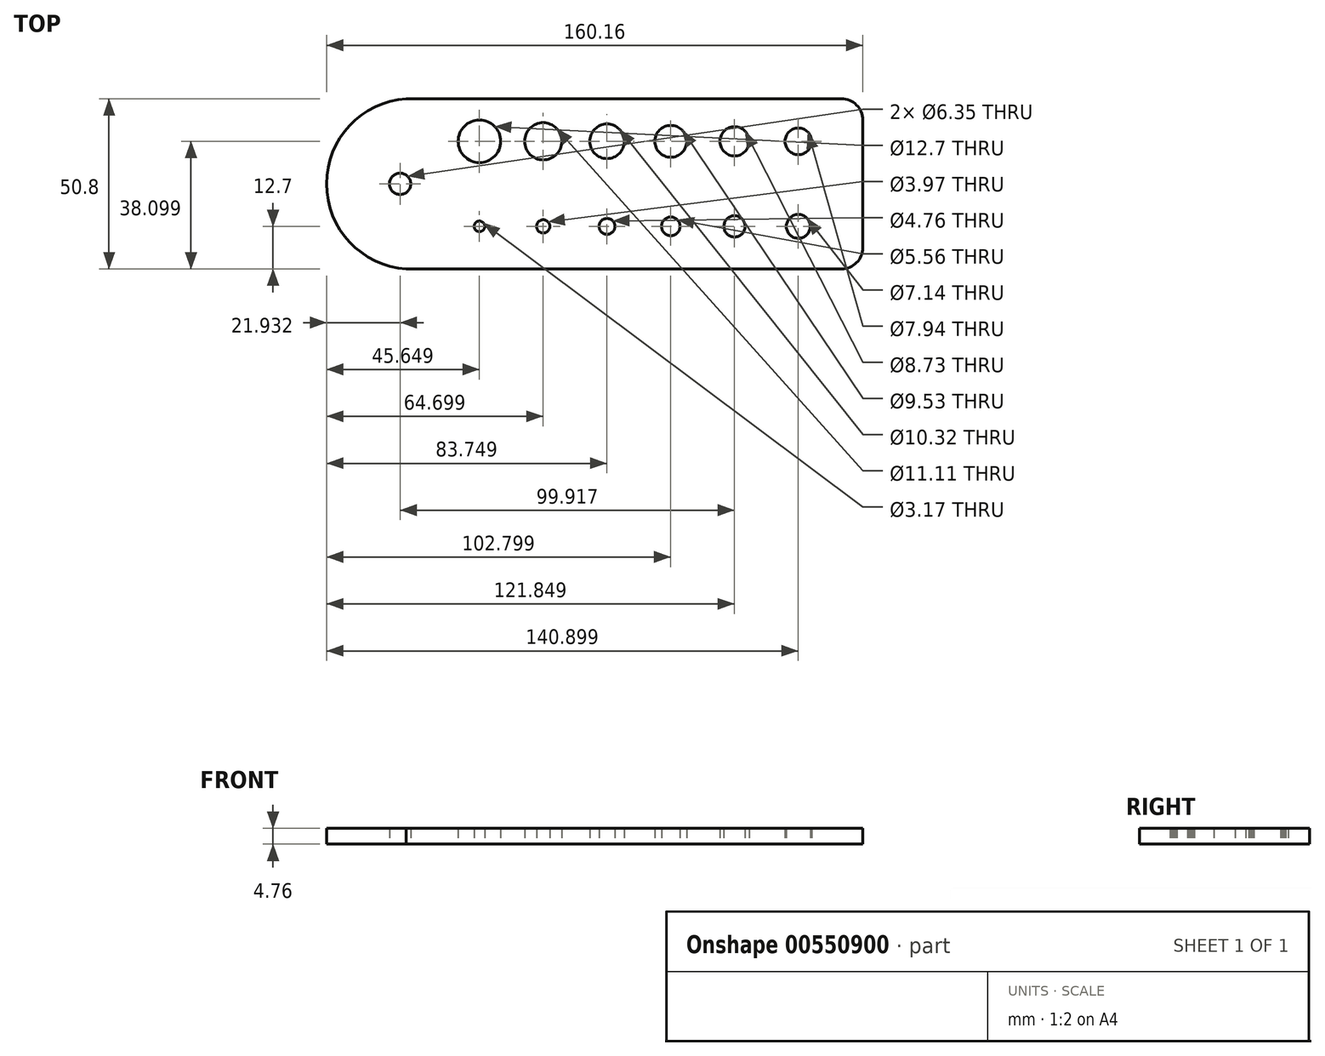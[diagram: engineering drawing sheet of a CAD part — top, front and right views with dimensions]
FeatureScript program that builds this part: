
annotation { "Feature Type Name" : "Feature", "Feature Type Description" : "" }
export const myFeature = defineFeature(function(context is Context, id is Id, definition is map)
    precondition{}
    {
        {
            var Q0;
            Q0=qCreatedBy(makeId("Top.planeOp"),FACE);
            var sketch = newSketch(context, id + "F0", { "sketchPlane" : qUnion([Q0])});
            skLineSegment(sketch, "E0.bottom", {"start": v(-46.8, 40.45) * mm, "end": v(83.22, 40.45) * mm});
            skLineSegment(sketch, "E0.top", {"start": v(-46.8, -10.35) * mm, "end": v(83.22, -10.35) * mm});
            skLineSegment(sketch, "E0.left", {"start": v(-62.83, 33.35) * mm, "end": v(-62.83, 33.35) * mm});
            skLineSegment(sketch, "E0.right", {"start": v(89.57, 34.1) * mm, "end": v(89.57, -4) * mm});
            skArc(sketch, "E1", {"start": v(-46.8, 40.45) * mm, "mid": v(-70.59, 15.05) * mm, "end": v(-46.8, -10.35) * mm});
            skPoint(sketch, "E2.visualSharp", {"position": v(89.57, -10.35) * mm});
            skArc(sketch, "E2.filletArc", {"start": v(83.22, -10.35) * mm, "mid": v(87.71, -8.5) * mm, "end": v(89.57, -4) * mm});
            skPoint(sketch, "E3.visualSharp", {"position": v(89.57, 40.45) * mm});
            skArc(sketch, "E3.filletArc", {"start": v(89.57, 34.1) * mm, "mid": v(87.71, 38.59) * mm, "end": v(83.22, 40.45) * mm});
            skSolve(sketch);
        }
        {
            var Q0;
            {var subQ5=sQuery(id+"F0.wireOp",EDGE,"E0.bottom");Q0=makeQuery(id+"F0.imprint","IMPRINT",FACE,{"disambiguationData":[TD([[makeQuery(id+"F0.imprint","IMPRINT",EDGE,{"derivedFrom":subQ5}),-1.0]])]});}
            var sketch = newSketch(context, id + "F1", { "sketchPlane" : qUnion([Q0])});
            skCircle(sketch, "E4", {"center": v(-24.94, 27.75) * mm, "radius": 6.35 * mm});
            skCircle(sketch, "E5", {"center": v(-5.9, 27.75) * mm, "radius": 5.56 * mm});
            skCircle(sketch, "E6", {"center": v(32.2, 27.75) * mm, "radius": 4.76 * mm});
            skCircle(sketch, "E7", {"center": v(51.26, 27.75) * mm, "radius": 4.37 * mm});
            skCircle(sketch, "E8", {"center": v(70.3, 27.75) * mm, "radius": 3.97 * mm});
            skCircle(sketch, "E9", {"center": v(13.16, 27.75) * mm, "radius": 5.16 * mm});
            skCircle(sketch, "E10", {"center": v(51.26, 2.35) * mm, "radius": 3.18 * mm});
            skCircle(sketch, "E11", {"center": v(32.2, 2.35) * mm, "radius": 2.78 * mm});
            skCircle(sketch, "E12", {"center": v(13.16, 2.35) * mm, "radius": 2.38 * mm});
            skCircle(sketch, "E13", {"center": v(70.3, 2.35) * mm, "radius": 3.57 * mm});
            skCircle(sketch, "E14", {"center": v(-5.9, 2.35) * mm, "radius": 1.98 * mm});
            skCircle(sketch, "E15", {"center": v(-24.94, 2.35) * mm, "radius": 1.59 * mm});
            skCircle(sketch, "E16", {"center": v(-48.66, 15.05) * mm, "radius": 3.18 * mm});
            skSolve(sketch);
        }
        {
            var Q0;
            Q0=qSketchRegion(id+"F0",true);
            extrude(context, id + "F2", {"entities" : qUnion([Q0]), "depth" : 4.76 * mm, "offsetDistance" : 25.4 * mm});
        }
        {
            var Q0;
            Q0=makeQuery(id+"F1.imprint","IMPRINT",FACE,{"disambiguationData":[TD([[makeQuery(id+"F1.imprint","IMPRINT",EDGE,{"derivedFrom":sQuery(id+"F1.wireOp",EDGE,"E4")}),1.0]])]});
            var Q1;
            Q1=makeQuery(id+"F1.imprint","IMPRINT",FACE,{"disambiguationData":[TD([[makeQuery(id+"F1.imprint","IMPRINT",EDGE,{"derivedFrom":sQuery(id+"F1.wireOp",EDGE,"E15")}),1.0]])]});
            var Q2;
            Q2=makeQuery(id+"F1.imprint","IMPRINT",FACE,{"disambiguationData":[TD([[makeQuery(id+"F1.imprint","IMPRINT",EDGE,{"derivedFrom":sQuery(id+"F1.wireOp",EDGE,"E16")}),1.0]])]});
            var Q3;
            Q3=makeQuery(id+"F1.imprint","IMPRINT",FACE,{"disambiguationData":[TD([[makeQuery(id+"F1.imprint","IMPRINT",EDGE,{"derivedFrom":sQuery(id+"F1.wireOp",EDGE,"E5")}),1.0]])]});
            var Q4;
            Q4=makeQuery(id+"F1.imprint","IMPRINT",FACE,{"disambiguationData":[TD([[makeQuery(id+"F1.imprint","IMPRINT",EDGE,{"derivedFrom":sQuery(id+"F1.wireOp",EDGE,"E9")}),1.0]])]});
            var Q5;
            Q5=makeQuery(id+"F1.imprint","IMPRINT",FACE,{"disambiguationData":[TD([[makeQuery(id+"F1.imprint","IMPRINT",EDGE,{"derivedFrom":sQuery(id+"F1.wireOp",EDGE,"E6")}),1.0]])]});
            var Q6;
            Q6=makeQuery(id+"F1.imprint","IMPRINT",FACE,{"disambiguationData":[TD([[makeQuery(id+"F1.imprint","IMPRINT",EDGE,{"derivedFrom":sQuery(id+"F1.wireOp",EDGE,"E7")}),1.0]])]});
            var Q7;
            Q7=makeQuery(id+"F1.imprint","IMPRINT",FACE,{"disambiguationData":[TD([[makeQuery(id+"F1.imprint","IMPRINT",EDGE,{"derivedFrom":sQuery(id+"F1.wireOp",EDGE,"E8")}),1.0]])]});
            var Q8;
            Q8=makeQuery(id+"F1.imprint","IMPRINT",FACE,{"disambiguationData":[TD([[makeQuery(id+"F1.imprint","IMPRINT",EDGE,{"derivedFrom":sQuery(id+"F1.wireOp",EDGE,"E13")}),1.0]])]});
            var Q9;
            Q9=makeQuery(id+"F1.imprint","IMPRINT",FACE,{"disambiguationData":[TD([[makeQuery(id+"F1.imprint","IMPRINT",EDGE,{"derivedFrom":sQuery(id+"F1.wireOp",EDGE,"E10")}),1.0]])]});
            var Q10;
            Q10=makeQuery(id+"F1.imprint","IMPRINT",FACE,{"disambiguationData":[TD([[makeQuery(id+"F1.imprint","IMPRINT",EDGE,{"derivedFrom":sQuery(id+"F1.wireOp",EDGE,"E11")}),1.0]])]});
            var Q11;
            Q11=makeQuery(id+"F1.imprint","IMPRINT",FACE,{"disambiguationData":[TD([[makeQuery(id+"F1.imprint","IMPRINT",EDGE,{"derivedFrom":sQuery(id+"F1.wireOp",EDGE,"E12")}),1.0]])]});
            var Q12;
            Q12=makeQuery(id+"F1.imprint","IMPRINT",FACE,{"disambiguationData":[TD([[makeQuery(id+"F1.imprint","IMPRINT",EDGE,{"derivedFrom":sQuery(id+"F1.wireOp",EDGE,"E14")}),1.0]])]});
            extrude(context, id + "F3", {"entities" : qUnion([Q0, Q1, Q2, Q3, Q4, Q5, Q6, Q7, Q8, Q9, Q10, Q11, Q12]), "operationType" : NewBodyOperationType.REMOVE, "depth" : 35.56 * mm, "offsetDistance" : 25.4 * mm});
        }
    });
